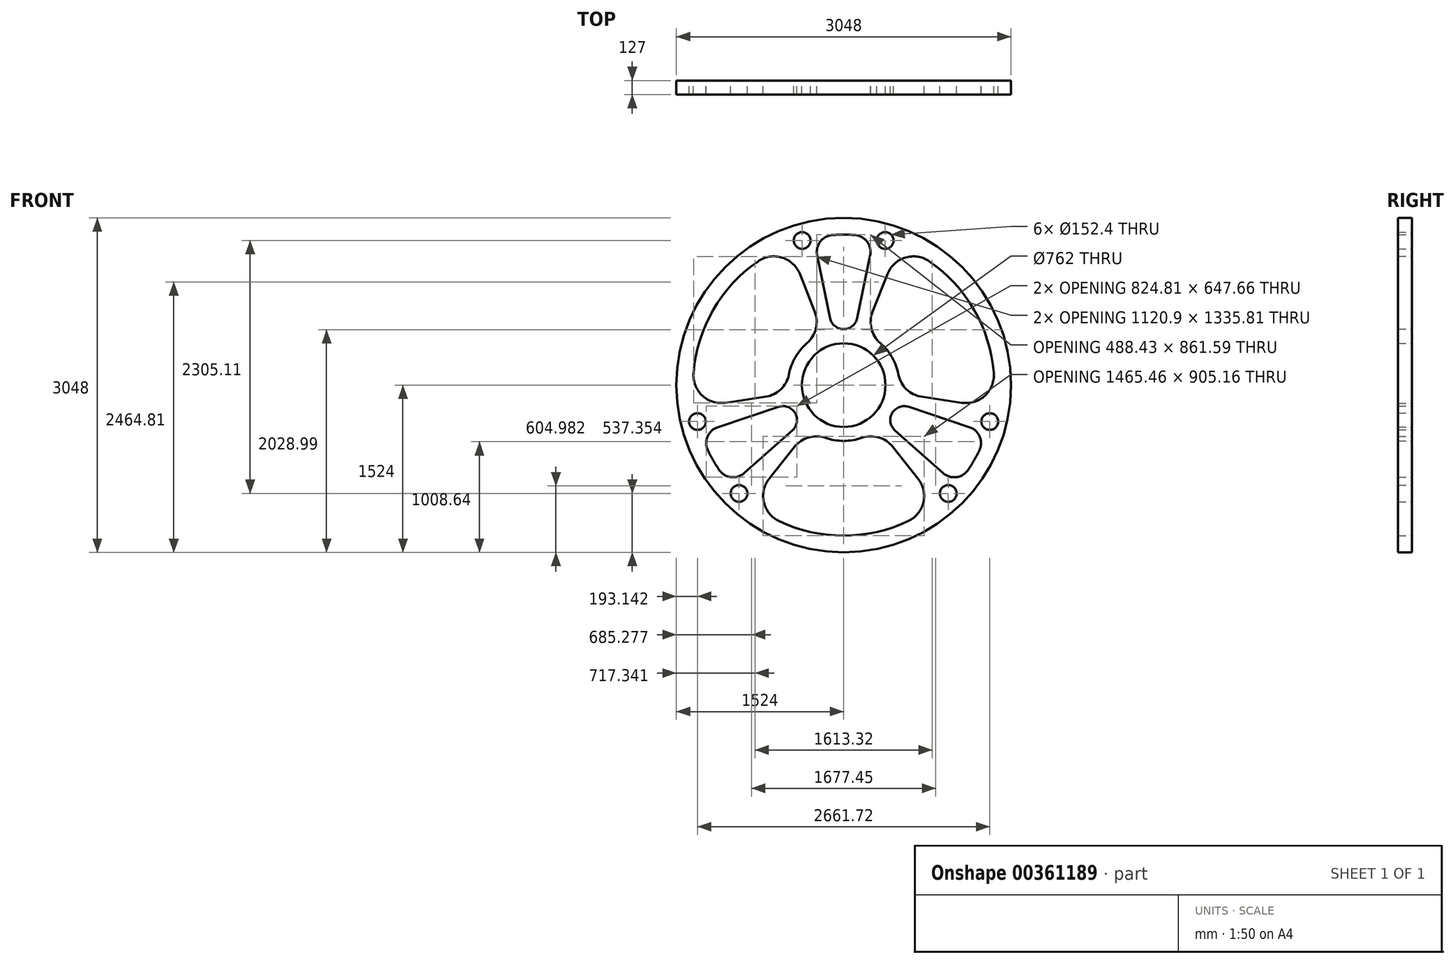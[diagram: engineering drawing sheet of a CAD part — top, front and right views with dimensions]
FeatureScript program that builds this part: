
annotation { "Feature Type Name" : "Feature", "Feature Type Description" : "" }
export const myFeature = defineFeature(function(context is Context, id is Id, definition is map)
    precondition{}
    {
        {
            var Q0;
            Q0=qCreatedBy(makeId("Front.planeOp"),FACE);
            var sketch = newSketch(context, id + "F0", { "sketchPlane" : qUnion([Q0])});
            skCircle(sketch, "E0", {"center": v(0, 0) * mm, "radius": 1524 * mm});
            skArc(sketch, "E1", {"start": v(-273.45, 1344.06) * mm, "mid": v(-288.88, 1340.83) * mm, "end": v(-304.26, 1337.43) * mm});
            skLineSegment(sketch, "E2", {"start": v(0, 508) * mm, "end": v(0, 510.01) * mm});
            skLineSegment(sketch, "E3", {"start": v(-124.45, 611.7) * mm, "end": v(-241.16, 1185.35) * mm});
            skLineSegment(sketch, "E4", {"start": v(124.45, 611.7) * mm, "end": v(241.16, 1185.35) * mm});
            skArc(sketch, "E5.trimOffspring", {"start": v(-103.3, 1367.7) * mm, "mid": v(-213.39, 1307.65) * mm, "end": v(-241.16, 1185.35) * mm});
            skArc(sketch, "E6.trimOffspring", {"start": v(241.16, 1185.35) * mm, "mid": v(213.39, 1307.65) * mm, "end": v(103.3, 1367.7) * mm});
            skArc(sketch, "E7.trimOffspring", {"start": v(103.3, 1367.7) * mm, "mid": v(0, 1371.6) * mm, "end": v(-103.3, 1367.7) * mm});
            skArc(sketch, "E8", {"start": v(-124.45, 611.7) * mm, "mid": v(0, 510.01) * mm, "end": v(124.45, 611.7) * mm});
            skLineSegment(sketch, "E9.1.0", {"start": v(-591.97, -198.07) * mm, "end": v(-1147.13, -383.82) * mm});
            skArc(sketch, "E9.1.1", {"start": v(-1147.13, -383.82) * mm, "mid": v(-1239.15, -469.02) * mm, "end": v(-1236.12, -594.4) * mm});
            skArc(sketch, "E9.1.3", {"start": v(-1132.82, -773.31) * mm, "mid": v(-1025.76, -838.62) * mm, "end": v(-905.96, -801.53) * mm});
            skLineSegment(sketch, "E9.1.4", {"start": v(-467.52, -413.62) * mm, "end": v(-905.96, -801.53) * mm});
            skArc(sketch, "E9.1.5", {"start": v(-467.52, -413.62) * mm, "mid": v(-441.68, -255) * mm, "end": v(-591.97, -198.07) * mm});
            skLineSegment(sketch, "E9.2.0", {"start": v(467.52, -413.62) * mm, "end": v(905.96, -801.53) * mm});
            skArc(sketch, "E9.2.1", {"start": v(905.96, -801.53) * mm, "mid": v(1025.76, -838.62) * mm, "end": v(1132.82, -773.31) * mm});
            skArc(sketch, "E9.2.2", {"start": v(1132.82, -773.31) * mm, "mid": v(1187.84, -685.8) * mm, "end": v(1236.12, -594.4) * mm});
            skArc(sketch, "E9.2.3", {"start": v(1236.12, -594.4) * mm, "mid": v(1239.15, -469.02) * mm, "end": v(1147.13, -383.82) * mm});
            skLineSegment(sketch, "E9.2.4", {"start": v(591.97, -198.07) * mm, "end": v(1147.13, -383.82) * mm});
            skArc(sketch, "E9.2.5", {"start": v(591.97, -198.07) * mm, "mid": v(441.68, -255) * mm, "end": v(467.52, -413.62) * mm});
            skLineSegment(sketch, "E10", {"start": v(378.06, 1318.47) * mm, "end": v(399.07, 1391.71) * mm});
            skLineSegment(sketch, "E11", {"start": v(-378.06, 1318.47) * mm, "end": v(-399.07, 1391.71) * mm});
            skCircle(sketch, "E12", {"center": v(378.06, 1318.47) * mm, "radius": 76.2 * mm});
            skCircle(sketch, "E13", {"center": v(-378.06, 1318.47) * mm, "radius": 76.2 * mm});
            skCircle(sketch, "E14.1.0", {"center": v(-1330.86, -331.82) * mm, "radius": 76.2 * mm});
            skCircle(sketch, "E14.1.1", {"center": v(-952.8, -986.65) * mm, "radius": 76.2 * mm});
            skCircle(sketch, "E14.2.0", {"center": v(952.8, -986.65) * mm, "radius": 76.2 * mm});
            skCircle(sketch, "E14.2.1", {"center": v(1330.86, -331.82) * mm, "radius": 76.2 * mm});
            skArc(sketch, "E15", {"start": v(-333.09, 383.56) * mm, "mid": v(-439.94, 254) * mm, "end": v(-498.72, 96.68) * mm});
            skArc(sketch, "E16", {"start": v(-677.52, -851.75) * mm, "mid": v(-726.16, -1067.3) * mm, "end": v(-587.54, -1239.39) * mm});
            skArc(sketch, "E17", {"start": v(587.54, -1239.39) * mm, "mid": v(726.16, -1067.3) * mm, "end": v(677.52, -851.75) * mm});
            skArc(sketch, "E18.trimOffspring", {"start": v(-165.63, -480.24) * mm, "mid": v(-319.46, -476.49) * mm, "end": v(-447.23, -562.24) * mm});
            skArc(sketch, "E19.trimOffspring", {"start": v(447.23, -562.24) * mm, "mid": v(319.46, -476.49) * mm, "end": v(165.63, -480.24) * mm});
            skArc(sketch, "E20.1.0", {"start": v(1076.4, -160.87) * mm, "mid": v(1287.4, -95.22) * mm, "end": v(1367.11, 110.87) * mm});
            skArc(sketch, "E20.1.2", {"start": v(779.57, 1128.52) * mm, "mid": v(561.24, 1162.52) * mm, "end": v(398.88, 1012.62) * mm});
            skArc(sketch, "E20.1.3", {"start": v(263.3, 668.43) * mm, "mid": v(252.92, 514.9) * mm, "end": v(333.09, 383.56) * mm});
            skLineSegment(sketch, "E20.1.4", {"start": v(263.3, 668.43) * mm, "end": v(398.88, 1012.62) * mm});
            skArc(sketch, "E20.1.5", {"start": v(498.72, 96.68) * mm, "mid": v(572.38, -38.42) * mm, "end": v(710.53, -106.19) * mm});
            skArc(sketch, "E20.1.7", {"start": v(-165.63, -480.24) * mm, "mid": v(0, -508) * mm, "end": v(165.63, -480.24) * mm});
            skArc(sketch, "E20.2.0", {"start": v(-398.88, 1012.62) * mm, "mid": v(-561.24, 1162.52) * mm, "end": v(-779.57, 1128.52) * mm});
            skArc(sketch, "E20.2.2", {"start": v(-1367.11, 110.87) * mm, "mid": v(-1287.4, -95.22) * mm, "end": v(-1076.4, -160.87) * mm});
            skArc(sketch, "E20.2.3", {"start": v(-710.53, -106.19) * mm, "mid": v(-572.38, -38.42) * mm, "end": v(-498.72, 96.68) * mm});
            skLineSegment(sketch, "E20.2.4", {"start": v(-710.53, -106.19) * mm, "end": v(-1076.4, -160.87) * mm});
            skArc(sketch, "E20.2.5", {"start": v(-333.09, 383.56) * mm, "mid": v(-252.92, 514.9) * mm, "end": v(-263.3, 668.43) * mm});
            skLineSegment(sketch, "E21.trimOffspring", {"start": v(-263.3, 668.43) * mm, "end": v(-398.88, 1012.62) * mm});
            skPoint(sketch, "E22.orphan", {"position": v(-1694.05, -253.18) * mm});
            skLineSegment(sketch, "E23.trimOffspring", {"start": v(447.23, -562.24) * mm, "end": v(677.52, -851.75) * mm});
            skLineSegment(sketch, "E24.trimOffspring", {"start": v(-447.23, -562.24) * mm, "end": v(-677.52, -851.75) * mm});
            skLineSegment(sketch, "E25.trimOffspring", {"start": v(710.53, -106.19) * mm, "end": v(1076.4, -160.87) * mm});
            skArc(sketch, "E26.trimOffspring", {"start": v(304.26, 1337.43) * mm, "mid": v(288.88, 1340.83) * mm, "end": v(273.45, 1344.06) * mm});
            skArc(sketch, "E27.trimOffspring", {"start": v(-779.57, 1128.52) * mm, "mid": v(-1187.84, 685.8) * mm, "end": v(-1367.11, 110.87) * mm});
            skArc(sketch, "E28.trimOffspring", {"start": v(1367.11, 110.87) * mm, "mid": v(1187.84, 685.8) * mm, "end": v(779.57, 1128.52) * mm});
            skPoint(sketch, "E29.orphan", {"position": v(1027.27, -908.85) * mm});
            skArc(sketch, "E30.trimOffspring", {"start": v(-587.54, -1239.39) * mm, "mid": v(0, -1371.6) * mm, "end": v(587.54, -1239.39) * mm});
            skArc(sketch, "E31.trimOffspring", {"start": v(-1236.12, -594.4) * mm, "mid": v(-1187.84, -685.8) * mm, "end": v(-1132.82, -773.31) * mm});
            skPoint(sketch, "E32.orphan", {"position": v(-1300.72, -435.22) * mm});
            skArc(sketch, "E33.trimOffspring", {"start": v(498.72, 96.68) * mm, "mid": v(439.94, 254) * mm, "end": v(333.09, 383.56) * mm});
            skCircle(sketch, "E34", {"center": v(0, 0) * mm, "radius": 381 * mm});
            skCircle(sketch, "E35", {"center": v(0, 152.4) * mm, "radius": 25.4 * mm});
            skCircle(sketch, "E36.1.0", {"center": v(-131.98, -76.2) * mm, "radius": 25.4 * mm});
            skCircle(sketch, "E36.2.0", {"center": v(131.98, -76.2) * mm, "radius": 25.4 * mm});
            skCircle(sketch, "E37", {"center": v(0, -152.4) * mm, "radius": 25.4 * mm});
            skCircle(sketch, "E38.1.0", {"center": v(131.98, 76.2) * mm, "radius": 25.4 * mm});
            skCircle(sketch, "E38.2.0", {"center": v(-131.98, 76.2) * mm, "radius": 25.4 * mm});
            skSolve(sketch);
        }
        {
            var Q0;
            Q0 = qSketchRegion(id + "F0", true);
            extrude(context, id + "F1", {"entities" : qUnion([Q0]), "depth" : 127 * mm});
        }
    });
